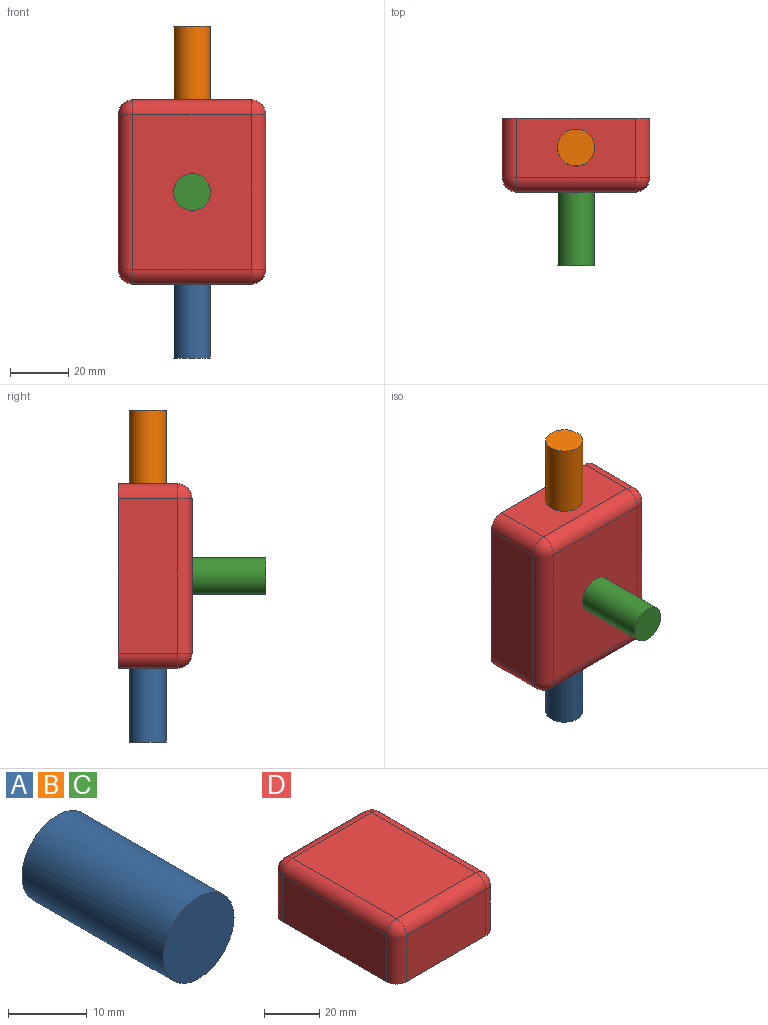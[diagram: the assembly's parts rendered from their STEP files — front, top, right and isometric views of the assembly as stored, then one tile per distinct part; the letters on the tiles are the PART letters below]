
ASSEMBLY  parts=4 mates=3
PART A: 3 faces, bbox 12.7x25.4x12.7 mm
  f0: cylinder r=6.35mm len=25.4mm, axis (0,1,0), area 1013.4mm2, adj f1,f2
  f1: plane 12.7x12.7mm, normal (0,-1,0), area 126.7mm2, adj f0
  f2: plane 12.7x12.7mm, normal (0,1,0), area 126.7mm2, adj f0
PART B: same geometry as A
PART C: same geometry as A
PART D: 18 faces, bbox 50.8x63.5x25.4 mm
  f0: plane 40.64x20.32mm, normal (0,1,0), area 825.8mm2, adj f5,f6,f10,f12
  f1: plane 53.34x20.32mm, normal (-1,0,0), area 1083.9mm2, adj f5,f7,f12,f14
  f2: plane 40.64x20.32mm, normal (0,-1,0), area 825.8mm2, adj f5,f9,f14,f16
  f3: plane 53.34x20.32mm, normal (1,0,0), area 1083.9mm2, adj f5,f8,f10,f16
  f4: plane 53.34x40.64mm, normal (0,0,1), area 2167.7mm2, adj f6,f7,f8,f9
  f5: plane 63.5x50.8mm, normal (0,0,-1), area 3203.6mm2, adj f0,f1,f2,f3,f10,f12,f14,f16
  f6: cylinder r=5.08mm len=40.64mm, axis (1,0,0), area 324.3mm2, adj f0,f4,f11,f13
  f7: cylinder r=5.08mm len=53.34mm, axis (0,1,0), area 425.6mm2, adj f1,f4,f13,f15
  f8: cylinder r=5.08mm len=53.34mm, axis (0,-1,0), area 425.6mm2, adj f3,f4,f11,f17
  f9: cylinder r=5.08mm len=40.64mm, axis (-1,0,0), area 324.3mm2, adj f2,f4,f15,f17
  f10: cylinder r=5.08mm len=20.32mm, axis (0,0,1), area 162.1mm2, adj f0,f3,f5,f11
  f11: sphere r=5.08mm, area 40.5mm2, adj f6,f8,f10
  f12: cylinder r=5.08mm len=20.32mm, axis (0,0,-1), area 162.1mm2, adj f0,f1,f5,f13
  f13: sphere r=5.08mm, area 40.5mm2, adj f6,f7,f12
  f14: cylinder r=5.08mm len=20.32mm, axis (0,0,1), area 162.1mm2, adj f1,f2,f5,f15
  f15: sphere r=5.08mm, area 40.5mm2, adj f7,f9,f14
  f16: cylinder r=5.08mm len=20.32mm, axis (0,0,-1), area 162.1mm2, adj f2,f3,f5,f17
  f17: sphere r=5.08mm, area 40.5mm2, adj f8,f9,f16
PLACE A rot(axis=(1,0,0),90deg) t=(-11.63,2.89,-65.95)mm
PLACE B rot(axis=(1,0,0),90deg) t=(-11.63,2.89,22.95)mm
PLACE C t=(-11.63,-5.68,-27.53)mm
PLACE D rot(axis=(1,0,0),90deg) t=(-97.74,19.72,-65.95)mm
MATE fastened D.f4 <-> C.f0  axis (0,-1,0) through (-72.34,-5.68,-34.2)mm
MATE fastened D.f0 <-> B.f0  axis (0,0,1) through (-72.34,9.56,-2.45)mm
MATE fastened D.f2 <-> A.f0  axis (0,0,-1) through (-72.34,9.56,-65.95)mm
